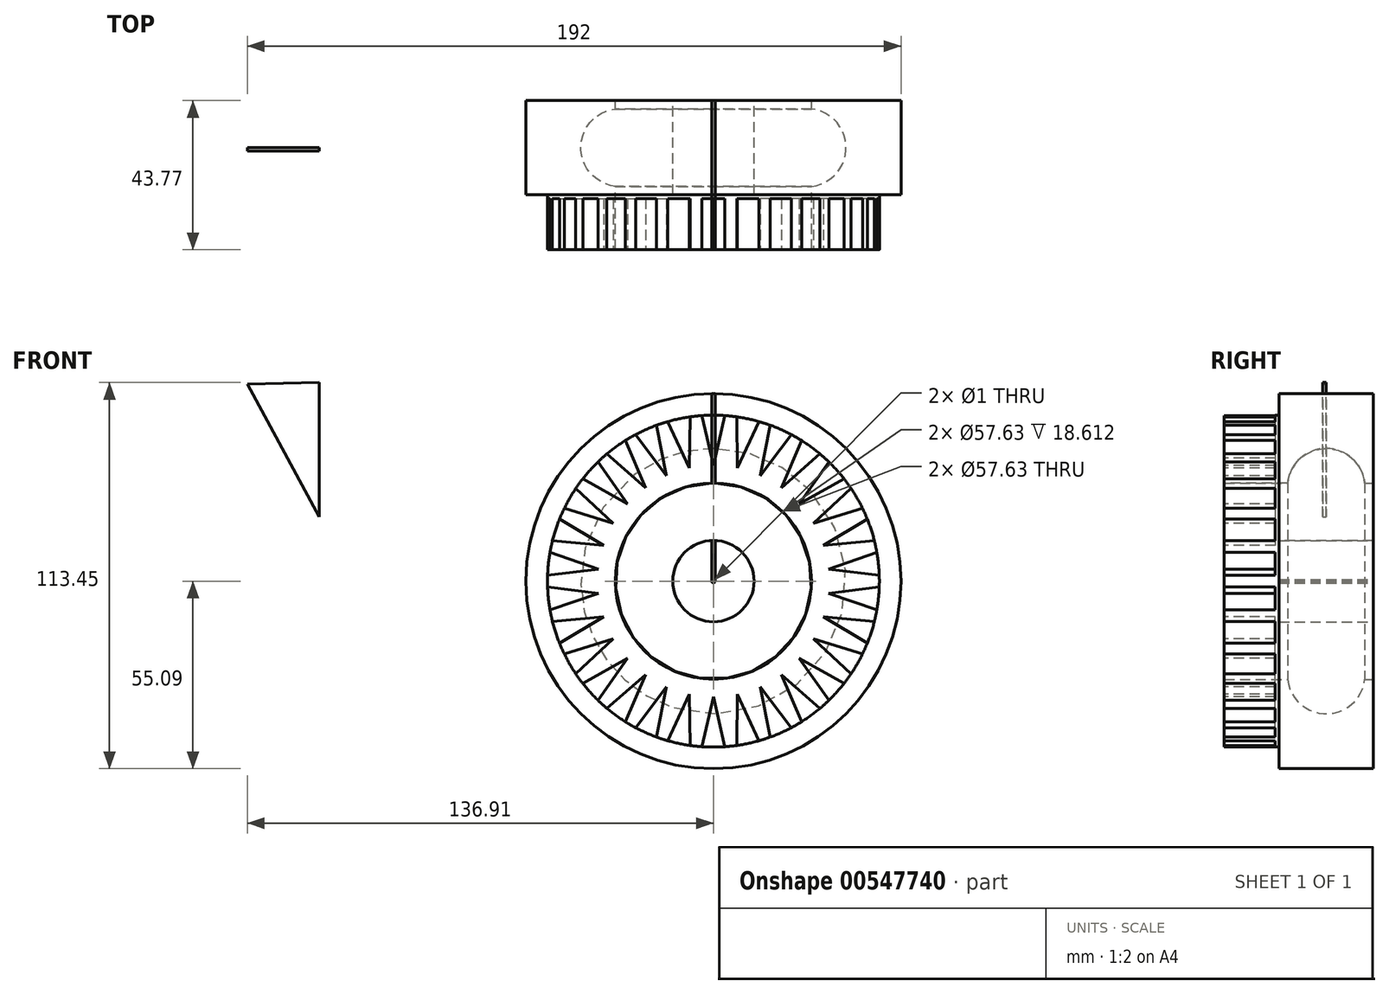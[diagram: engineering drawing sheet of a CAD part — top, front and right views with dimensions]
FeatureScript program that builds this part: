
annotation { "Feature Type Name" : "Feature", "Feature Type Description" : "" }
export const myFeature = defineFeature(function(context is Context, id is Id, definition is map)
    precondition{}
    {
        {
            var Q0;
            Q0=qCreatedBy(makeId("Right.planeOp"),FACE);
            var sketch = newSketch(context, id + "F0", { "sketchPlane" : qUnion([Q0])});
            skLineSegment(sketch, "E0.bottom", {"start": v(0, 0) * mm, "end": v(13.82, 0) * mm});
            skLineSegment(sketch, "E0.top", {"start": v(0, 26.27) * mm, "end": v(13.82, 26.27) * mm});
            skLineSegment(sketch, "E0.left", {"start": v(0, 0) * mm, "end": v(0, 26.27) * mm});
            skLineSegment(sketch, "E0.right", {"start": v(13.82, 0) * mm, "end": v(13.82, 26.27) * mm});
            skLineSegment(sketch, "E1.MirrorCS", {"start": v(0, 26.27) * mm, "end": v(-13.82, 26.27) * mm});
            skLineSegment(sketch, "E2.MirrorCS", {"start": v(-13.82, 0) * mm, "end": v(-13.82, 26.27) * mm});
            skLineSegment(sketch, "E3.MirrorCS", {"start": v(0, 0) * mm, "end": v(-13.82, 0) * mm});
            skCircle(sketch, "E4", {"center": v(0, 27.54) * mm, "radius": 11.41 * mm});
            skLineSegment(sketch, "E5.MirrorCS", {"start": v(0, 28.81) * mm, "end": v(-13.82, 28.81) * mm});
            skLineSegment(sketch, "E6.MirrorCS", {"start": v(-13.82, 55.09) * mm, "end": v(-13.82, 28.81) * mm});
            skLineSegment(sketch, "E7.MirrorCS", {"start": v(0, 28.81) * mm, "end": v(13.82, 28.81) * mm});
            skLineSegment(sketch, "E8.MirrorCS", {"start": v(13.82, 55.09) * mm, "end": v(13.82, 28.81) * mm});
            skLineSegment(sketch, "E9.MirrorCS", {"start": v(0, 55.09) * mm, "end": v(13.82, 55.09) * mm});
            skLineSegment(sketch, "E10.MirrorCS", {"start": v(0, 55.09) * mm, "end": v(-13.82, 55.09) * mm});
            skLineSegment(sketch, "E11", {"start": v(-13.82, 28.81) * mm, "end": v(-29.95, 28.81) * mm});
            skLineSegment(sketch, "E12", {"start": v(-29.95, 28.81) * mm, "end": v(-29.95, 48.74) * mm});
            skLineSegment(sketch, "E13", {"start": v(-29.95, 48.74) * mm, "end": v(-13.82, 48.74) * mm});
            skLineSegment(sketch, "E14", {"start": v(-13.82, 55.09) * mm, "end": v(-13.82, 48.74) * mm});
            skLineSegment(sketch, "E15.bottom", {"start": v(13.82, 11.94) * mm, "end": v(-13.82, 11.94) * mm});
            skLineSegment(sketch, "E15.top", {"start": v(13.82, -11.94) * mm, "end": v(-13.82, -11.94) * mm});
            skLineSegment(sketch, "E15.left", {"start": v(13.82, 11.94) * mm, "end": v(13.82, -11.94) * mm});
            skLineSegment(sketch, "E15.right", {"start": v(-13.82, 11.94) * mm, "end": v(-13.82, -11.94) * mm});
            skPoint(sketch, "E15.middle", {"position": v(0, 0) * mm});
            skSolve(sketch);
        }
        {
            var Q0;
            Q0=qCreatedBy(makeId("Right.planeOp"),FACE);
            var sketch = newSketch(context, id + "F1", { "sketchPlane" : qUnion([Q0])});
            skLineSegment(sketch, "E16", {"start": v(13.71, 0) * mm, "end": v(-13.92, 0) * mm, "construction": true});
            skSolve(sketch);
        }
        {
            var Q0;
            {var subQ0=sQuery(id+"F0.wireOp",EDGE,"E0.right");Q0=makeQuery(id+"F0.imprint","IMPRINT",FACE,{"disambiguationData":[TD([[makeQuery(id+"F0.imprint","IMPRINT",EDGE,{"derivedFrom":subQ0}),1.0]])]});}
            var Q1;
            {var subQ5=sQuery(id+"F0.wireOp",EDGE,"E2.MirrorCS");Q1=makeQuery(id+"F0.imprint","IMPRINT",FACE,{"disambiguationData":[TD([[makeQuery(id+"F0.imprint","IMPRINT",EDGE,{"derivedFrom":subQ5}),-1.0]])]});}
            var Q2;
            Q2=makeQuery(id+"F0.imprint","IMPRINT",FACE,{"disambiguationData":[TD([[makeQuery(id+"F0.imprint","IMPRINT",EDGE,{"derivedFrom":sQuery(id+"F0.wireOp",EDGE,"E6.MirrorCS")}),-1.0]])]});
            var Q3;
            {var subQ4=sQuery(id+"F0.wireOp",EDGE,"E6.MirrorCS");Q3=makeQuery(id+"F0.imprint","IMPRINT",FACE,{"disambiguationData":[TD([[makeQuery(id+"F0.imprint","IMPRINT",EDGE,{"derivedFrom":subQ4}),1.0]])]});}
            extrude(context, id + "F2", {"entities" : qUnion([Q0, Q1, Q2, Q3]), "endBound" : BoundingType.SYMMETRIC, "depth" : 1 * mm, "offsetDistance" : 25 * mm});
        }
        {
            var Q0;
            Q0=makeQuery(id+"F2.opExtrude","CAP_FACE",FACE,{"disambiguationData":[OSD([sQuery(id+"F0.wireOp",EDGE,"E4"),sQuery(id+"F0.wireOp",EDGE,"E5.MirrorCS"),sQuery(id+"F0.wireOp",EDGE,"E7.MirrorCS"),sQuery(id+"F0.wireOp",EDGE,"E8.MirrorCS"),sQuery(id+"F0.wireOp",EDGE,"E9.MirrorCS"),sQuery(id+"F0.wireOp",EDGE,"E10.MirrorCS"),sQuery(id+"F0.wireOp",EDGE,"E11"),sQuery(id+"F0.wireOp",EDGE,"E12"),sQuery(id+"F0.wireOp",EDGE,"E13"),sQuery(id+"F0.wireOp",EDGE,"E14")])],"isStart":true});
            var Q1;
            Q1=makeQuery(id+"F2.opExtrude","CAP_FACE",FACE,{"disambiguationData":[OSD([sQuery(id+"F0.wireOp",EDGE,"E0.top"),sQuery(id+"F0.wireOp",EDGE,"E0.right"),sQuery(id+"F0.wireOp",EDGE,"E1.MirrorCS"),sQuery(id+"F0.wireOp",EDGE,"E2.MirrorCS"),sQuery(id+"F0.wireOp",EDGE,"E4"),sQuery(id+"F0.wireOp",EDGE,"E15.bottom")])],"isStart":true});
            var Q2;
            Q2=sQuery(id+"F1.wireOp",EDGE,"E16");
            revolve(context, id + "F3", {"entities" : qUnion([Q0, Q1]), "axis" : qUnion([Q2]), "revolveType" : RevolveType.FULL});
        }
        {
            var Q0;
            Q0=makeQuery(id+"F3.opRevolve","SWEPT_FACE",FACE,{"disambiguationData":[OSD([sQuery(id+"F0.wireOp",EDGE,"E12")])]});
            var sketch = newSketch(context, id + "F4", { "sketchPlane" : qUnion([Q0])});
            skLineSegment(sketch, "E17", {"start": v(0, 48.74) * mm, "end": v(-3.37, 48.74) * mm});
            skLineSegment(sketch, "E18", {"start": v(-3.37, 48.74) * mm, "end": v(0, 33.93) * mm});
            skLineSegment(sketch, "E19.MirrorCS", {"start": v(0, 48.74) * mm, "end": v(3.37, 48.74) * mm});
            skPoint(sketch, "E20.center", {"position": v(0, 0) * mm});
            skLineSegment(sketch, "E21.MirrorCS", {"start": v(3.37, 48.74) * mm, "end": v(0, 33.93) * mm});
            skLineSegment(sketch, "E22.1.0", {"start": v(-6.84, 48.37) * mm, "end": v(-7.05, 33.2) * mm});
            skLineSegment(sketch, "E22.1.1", {"start": v(-13.43, 46.97) * mm, "end": v(-7.05, 33.2) * mm});
            skLineSegment(sketch, "E22.1.2", {"start": v(-10.13, 47.67) * mm, "end": v(-6.84, 48.37) * mm});
            skLineSegment(sketch, "E22.1.3", {"start": v(-10.13, 47.67) * mm, "end": v(-13.43, 46.97) * mm});
            skLineSegment(sketch, "E22.2.0", {"start": v(-16.74, 45.9) * mm, "end": v(-13.8, 31) * mm});
            skLineSegment(sketch, "E22.2.1", {"start": v(-22.9, 43.15) * mm, "end": v(-13.8, 31) * mm});
            skLineSegment(sketch, "E22.2.2", {"start": v(-19.82, 44.53) * mm, "end": v(-16.74, 45.9) * mm});
            skLineSegment(sketch, "E22.2.3", {"start": v(-19.82, 44.53) * mm, "end": v(-22.9, 43.15) * mm});
            skLineSegment(sketch, "E23.2.3.0", {"start": v(-25.92, 41.41) * mm, "end": v(-19.94, 27.45) * mm});
            skLineSegment(sketch, "E23.3.3.0", {"start": v(-31.38, 37.45) * mm, "end": v(-19.94, 27.45) * mm});
            skLineSegment(sketch, "E23.6.3.0", {"start": v(-28.65, 39.43) * mm, "end": v(-25.92, 41.41) * mm});
            skLineSegment(sketch, "E23.9.3.0", {"start": v(-28.65, 39.43) * mm, "end": v(-31.38, 37.45) * mm});
            skLineSegment(sketch, "E23.2.4.0", {"start": v(-33.96, 35.12) * mm, "end": v(-25.22, 22.7) * mm});
            skLineSegment(sketch, "E23.3.4.0", {"start": v(-38.48, 30.1) * mm, "end": v(-25.22, 22.7) * mm});
            skLineSegment(sketch, "E23.6.4.0", {"start": v(-36.22, 32.61) * mm, "end": v(-33.96, 35.12) * mm});
            skLineSegment(sketch, "E23.9.4.0", {"start": v(-36.22, 32.61) * mm, "end": v(-38.48, 30.1) * mm});
            skLineSegment(sketch, "E23.2.5.0", {"start": v(-40.52, 27.29) * mm, "end": v(-29.39, 16.97) * mm});
            skLineSegment(sketch, "E23.3.5.0", {"start": v(-43.9, 21.45) * mm, "end": v(-29.39, 16.97) * mm});
            skLineSegment(sketch, "E23.6.5.0", {"start": v(-42.2, 24.37) * mm, "end": v(-40.52, 27.29) * mm});
            skLineSegment(sketch, "E23.9.5.0", {"start": v(-42.2, 24.37) * mm, "end": v(-43.9, 21.45) * mm});
            skLineSegment(sketch, "E23.2.6.0", {"start": v(-45.31, 18.27) * mm, "end": v(-32.27, 10.49) * mm});
            skLineSegment(sketch, "E23.3.6.0", {"start": v(-47.4, 11.86) * mm, "end": v(-32.27, 10.49) * mm});
            skLineSegment(sketch, "E23.6.6.0", {"start": v(-46.35, 15.06) * mm, "end": v(-45.31, 18.27) * mm});
            skLineSegment(sketch, "E23.9.6.0", {"start": v(-46.35, 15.06) * mm, "end": v(-47.4, 11.86) * mm});
            skLineSegment(sketch, "E23.2.7.0", {"start": v(-48.12, 8.45) * mm, "end": v(-33.75, 3.55) * mm});
            skLineSegment(sketch, "E23.3.7.0", {"start": v(-48.82, 1.74) * mm, "end": v(-33.75, 3.55) * mm});
            skLineSegment(sketch, "E23.6.7.0", {"start": v(-48.47, 5.1) * mm, "end": v(-48.12, 8.45) * mm});
            skLineSegment(sketch, "E23.9.7.0", {"start": v(-48.47, 5.1) * mm, "end": v(-48.82, 1.74) * mm});
            skLineSegment(sketch, "E23.2.8.0", {"start": v(-48.82, -1.74) * mm, "end": v(-33.75, -3.55) * mm});
            skLineSegment(sketch, "E23.3.8.0", {"start": v(-48.12, -8.45) * mm, "end": v(-33.75, -3.55) * mm});
            skLineSegment(sketch, "E23.6.8.0", {"start": v(-48.47, -5.1) * mm, "end": v(-48.82, -1.74) * mm});
            skLineSegment(sketch, "E23.9.8.0", {"start": v(-48.47, -5.1) * mm, "end": v(-48.12, -8.45) * mm});
            skLineSegment(sketch, "E23.2.9.0", {"start": v(-47.4, -11.86) * mm, "end": v(-32.27, -10.49) * mm});
            skLineSegment(sketch, "E23.3.9.0", {"start": v(-45.31, -18.27) * mm, "end": v(-32.27, -10.49) * mm});
            skLineSegment(sketch, "E23.6.9.0", {"start": v(-46.35, -15.06) * mm, "end": v(-47.4, -11.86) * mm});
            skLineSegment(sketch, "E23.9.9.0", {"start": v(-46.35, -15.06) * mm, "end": v(-45.31, -18.27) * mm});
            skLineSegment(sketch, "E23.2.10.0", {"start": v(-43.9, -21.45) * mm, "end": v(-29.39, -16.97) * mm});
            skLineSegment(sketch, "E23.3.10.0", {"start": v(-40.52, -27.29) * mm, "end": v(-29.39, -16.97) * mm});
            skLineSegment(sketch, "E23.6.10.0", {"start": v(-42.2, -24.37) * mm, "end": v(-43.9, -21.45) * mm});
            skLineSegment(sketch, "E23.9.10.0", {"start": v(-42.2, -24.37) * mm, "end": v(-40.52, -27.29) * mm});
            skLineSegment(sketch, "E23.2.11.0", {"start": v(-38.48, -30.1) * mm, "end": v(-25.22, -22.7) * mm});
            skLineSegment(sketch, "E23.3.11.0", {"start": v(-33.96, -35.12) * mm, "end": v(-25.22, -22.7) * mm});
            skLineSegment(sketch, "E23.6.11.0", {"start": v(-36.22, -32.61) * mm, "end": v(-38.48, -30.1) * mm});
            skLineSegment(sketch, "E23.9.11.0", {"start": v(-36.22, -32.61) * mm, "end": v(-33.96, -35.12) * mm});
            skLineSegment(sketch, "E23.2.12.0", {"start": v(-31.38, -37.45) * mm, "end": v(-19.94, -27.45) * mm});
            skLineSegment(sketch, "E23.3.12.0", {"start": v(-25.92, -41.41) * mm, "end": v(-19.94, -27.45) * mm});
            skLineSegment(sketch, "E23.6.12.0", {"start": v(-28.65, -39.43) * mm, "end": v(-31.38, -37.45) * mm});
            skLineSegment(sketch, "E23.9.12.0", {"start": v(-28.65, -39.43) * mm, "end": v(-25.92, -41.41) * mm});
            skLineSegment(sketch, "E23.2.13.0", {"start": v(-22.9, -43.15) * mm, "end": v(-13.8, -31) * mm});
            skLineSegment(sketch, "E23.3.13.0", {"start": v(-16.74, -45.9) * mm, "end": v(-13.8, -31) * mm});
            skLineSegment(sketch, "E23.6.13.0", {"start": v(-19.82, -44.53) * mm, "end": v(-22.9, -43.15) * mm});
            skLineSegment(sketch, "E23.9.13.0", {"start": v(-19.82, -44.53) * mm, "end": v(-16.74, -45.9) * mm});
            skLineSegment(sketch, "E23.2.14.0", {"start": v(-13.43, -46.97) * mm, "end": v(-7.05, -33.2) * mm});
            skLineSegment(sketch, "E23.3.14.0", {"start": v(-6.84, -48.37) * mm, "end": v(-7.05, -33.2) * mm});
            skLineSegment(sketch, "E23.6.14.0", {"start": v(-10.13, -47.67) * mm, "end": v(-13.43, -46.97) * mm});
            skLineSegment(sketch, "E23.9.14.0", {"start": v(-10.13, -47.67) * mm, "end": v(-6.84, -48.37) * mm});
            skLineSegment(sketch, "E23.2.15.0", {"start": v(-3.37, -48.74) * mm, "end": v(0, -33.93) * mm});
            skLineSegment(sketch, "E23.3.15.0", {"start": v(3.37, -48.74) * mm, "end": v(0, -33.93) * mm});
            skLineSegment(sketch, "E23.6.15.0", {"start": v(0, -48.74) * mm, "end": v(-3.37, -48.74) * mm});
            skLineSegment(sketch, "E23.9.15.0", {"start": v(0, -48.74) * mm, "end": v(3.37, -48.74) * mm});
            skLineSegment(sketch, "E23.2.16.0", {"start": v(6.84, -48.37) * mm, "end": v(7.05, -33.2) * mm});
            skLineSegment(sketch, "E23.3.16.0", {"start": v(13.43, -46.97) * mm, "end": v(7.05, -33.2) * mm});
            skLineSegment(sketch, "E23.6.16.0", {"start": v(10.13, -47.67) * mm, "end": v(6.84, -48.37) * mm});
            skLineSegment(sketch, "E23.9.16.0", {"start": v(10.13, -47.67) * mm, "end": v(13.43, -46.97) * mm});
            skLineSegment(sketch, "E23.2.17.0", {"start": v(16.74, -45.9) * mm, "end": v(13.8, -31) * mm});
            skLineSegment(sketch, "E23.3.17.0", {"start": v(22.9, -43.15) * mm, "end": v(13.8, -31) * mm});
            skLineSegment(sketch, "E23.6.17.0", {"start": v(19.82, -44.53) * mm, "end": v(16.74, -45.9) * mm});
            skLineSegment(sketch, "E23.9.17.0", {"start": v(19.82, -44.53) * mm, "end": v(22.9, -43.15) * mm});
            skLineSegment(sketch, "E23.2.18.0", {"start": v(25.92, -41.41) * mm, "end": v(19.94, -27.45) * mm});
            skLineSegment(sketch, "E23.3.18.0", {"start": v(31.38, -37.45) * mm, "end": v(19.94, -27.45) * mm});
            skLineSegment(sketch, "E23.6.18.0", {"start": v(28.65, -39.43) * mm, "end": v(25.92, -41.41) * mm});
            skLineSegment(sketch, "E23.9.18.0", {"start": v(28.65, -39.43) * mm, "end": v(31.38, -37.45) * mm});
            skLineSegment(sketch, "E23.2.19.0", {"start": v(33.96, -35.12) * mm, "end": v(25.22, -22.7) * mm});
            skLineSegment(sketch, "E23.3.19.0", {"start": v(38.48, -30.1) * mm, "end": v(25.22, -22.7) * mm});
            skLineSegment(sketch, "E23.6.19.0", {"start": v(36.22, -32.61) * mm, "end": v(33.96, -35.12) * mm});
            skLineSegment(sketch, "E23.9.19.0", {"start": v(36.22, -32.61) * mm, "end": v(38.48, -30.1) * mm});
            skLineSegment(sketch, "E23.2.20.0", {"start": v(40.52, -27.29) * mm, "end": v(29.39, -16.97) * mm});
            skLineSegment(sketch, "E23.3.20.0", {"start": v(43.9, -21.45) * mm, "end": v(29.39, -16.97) * mm});
            skLineSegment(sketch, "E23.6.20.0", {"start": v(42.2, -24.37) * mm, "end": v(40.52, -27.29) * mm});
            skLineSegment(sketch, "E23.9.20.0", {"start": v(42.2, -24.37) * mm, "end": v(43.9, -21.45) * mm});
            skLineSegment(sketch, "E23.2.21.0", {"start": v(45.31, -18.27) * mm, "end": v(32.27, -10.49) * mm});
            skLineSegment(sketch, "E23.3.21.0", {"start": v(47.4, -11.86) * mm, "end": v(32.27, -10.49) * mm});
            skLineSegment(sketch, "E23.6.21.0", {"start": v(46.35, -15.06) * mm, "end": v(45.31, -18.27) * mm});
            skLineSegment(sketch, "E23.9.21.0", {"start": v(46.35, -15.06) * mm, "end": v(47.4, -11.86) * mm});
            skLineSegment(sketch, "E23.2.22.0", {"start": v(48.12, -8.45) * mm, "end": v(33.75, -3.55) * mm});
            skLineSegment(sketch, "E23.3.22.0", {"start": v(48.82, -1.74) * mm, "end": v(33.75, -3.55) * mm});
            skLineSegment(sketch, "E23.6.22.0", {"start": v(48.47, -5.1) * mm, "end": v(48.12, -8.45) * mm});
            skLineSegment(sketch, "E23.9.22.0", {"start": v(48.47, -5.1) * mm, "end": v(48.82, -1.74) * mm});
            skLineSegment(sketch, "E23.2.23.0", {"start": v(48.82, 1.74) * mm, "end": v(33.75, 3.55) * mm});
            skLineSegment(sketch, "E23.3.23.0", {"start": v(48.12, 8.45) * mm, "end": v(33.75, 3.55) * mm});
            skLineSegment(sketch, "E23.6.23.0", {"start": v(48.47, 5.1) * mm, "end": v(48.82, 1.74) * mm});
            skLineSegment(sketch, "E23.9.23.0", {"start": v(48.47, 5.1) * mm, "end": v(48.12, 8.45) * mm});
            skLineSegment(sketch, "E23.2.24.0", {"start": v(47.4, 11.86) * mm, "end": v(32.27, 10.49) * mm});
            skLineSegment(sketch, "E23.3.24.0", {"start": v(45.31, 18.27) * mm, "end": v(32.27, 10.49) * mm});
            skLineSegment(sketch, "E23.6.24.0", {"start": v(46.35, 15.06) * mm, "end": v(47.4, 11.86) * mm});
            skLineSegment(sketch, "E23.9.24.0", {"start": v(46.35, 15.06) * mm, "end": v(45.31, 18.27) * mm});
            skLineSegment(sketch, "E23.2.25.0", {"start": v(43.9, 21.45) * mm, "end": v(29.39, 16.97) * mm});
            skLineSegment(sketch, "E23.3.25.0", {"start": v(40.52, 27.29) * mm, "end": v(29.39, 16.97) * mm});
            skLineSegment(sketch, "E23.6.25.0", {"start": v(42.2, 24.37) * mm, "end": v(43.9, 21.45) * mm});
            skLineSegment(sketch, "E23.9.25.0", {"start": v(42.2, 24.37) * mm, "end": v(40.52, 27.29) * mm});
            skLineSegment(sketch, "E23.2.26.0", {"start": v(38.48, 30.1) * mm, "end": v(25.22, 22.7) * mm});
            skLineSegment(sketch, "E23.3.26.0", {"start": v(33.96, 35.12) * mm, "end": v(25.22, 22.7) * mm});
            skLineSegment(sketch, "E23.6.26.0", {"start": v(36.22, 32.61) * mm, "end": v(38.48, 30.1) * mm});
            skLineSegment(sketch, "E23.9.26.0", {"start": v(36.22, 32.61) * mm, "end": v(33.96, 35.12) * mm});
            skLineSegment(sketch, "E23.2.27.0", {"start": v(31.38, 37.45) * mm, "end": v(19.94, 27.45) * mm});
            skLineSegment(sketch, "E23.3.27.0", {"start": v(25.92, 41.41) * mm, "end": v(19.94, 27.45) * mm});
            skLineSegment(sketch, "E23.6.27.0", {"start": v(28.65, 39.43) * mm, "end": v(31.38, 37.45) * mm});
            skLineSegment(sketch, "E23.9.27.0", {"start": v(28.65, 39.43) * mm, "end": v(25.92, 41.41) * mm});
            skLineSegment(sketch, "E23.2.28.0", {"start": v(22.9, 43.15) * mm, "end": v(13.8, 31) * mm});
            skLineSegment(sketch, "E23.3.28.0", {"start": v(16.74, 45.9) * mm, "end": v(13.8, 31) * mm});
            skLineSegment(sketch, "E23.6.28.0", {"start": v(19.82, 44.53) * mm, "end": v(22.9, 43.15) * mm});
            skLineSegment(sketch, "E23.9.28.0", {"start": v(19.82, 44.53) * mm, "end": v(16.74, 45.9) * mm});
            skLineSegment(sketch, "E23.2.29.0", {"start": v(13.43, 46.97) * mm, "end": v(7.05, 33.2) * mm});
            skLineSegment(sketch, "E23.3.29.0", {"start": v(6.84, 48.37) * mm, "end": v(7.05, 33.2) * mm});
            skLineSegment(sketch, "E23.6.29.0", {"start": v(10.13, 47.67) * mm, "end": v(13.43, 46.97) * mm});
            skLineSegment(sketch, "E23.9.29.0", {"start": v(10.13, 47.67) * mm, "end": v(6.84, 48.37) * mm});
            skSolve(sketch);
        }
        {
            var Q0;
            {var subQ0=sQuery(id+"F4.wireOp",EDGE,"E22.1.1");var subQ1=sQuery(id+"F4.wireOp",EDGE,"E22.1.0");var subQ2=makeQuery(id+"F4.imprint","INTERSECT",VERTEX,{"derivedFrom":[subQ1,subQ0]});Q0=makeQuery(id+"F4.imprint","IMPRINT",FACE,{"disambiguationData":[TD([[makeQuery(id+"F4.imprint","IMPRINT",EDGE,{"disambiguationData":[TD([[subQ2,1.0]])],"derivedFrom":subQ1}),-1.0]])]});}
            var Q1;
            {var subQ0=sQuery(id+"F4.wireOp",EDGE,"E21.MirrorCS");var subQ1=sQuery(id+"F4.wireOp",EDGE,"E18");var subQ2=makeQuery(id+"F4.imprint","INTERSECT",VERTEX,{"derivedFrom":[subQ1,subQ0]});Q1=makeQuery(id+"F4.imprint","IMPRINT",FACE,{"disambiguationData":[TD([[makeQuery(id+"F4.imprint","IMPRINT",EDGE,{"disambiguationData":[TD([[subQ2,1.0]])],"derivedFrom":subQ1}),1.0]])]});}
            var Q2;
            {var subQ0=sQuery(id+"F4.wireOp",EDGE,"E23.3.29.0");var subQ1=sQuery(id+"F4.wireOp",EDGE,"E23.2.29.0");var subQ2=makeQuery(id+"F4.imprint","INTERSECT",VERTEX,{"derivedFrom":[subQ1,subQ0]});Q2=makeQuery(id+"F4.imprint","IMPRINT",FACE,{"disambiguationData":[TD([[makeQuery(id+"F4.imprint","IMPRINT",EDGE,{"disambiguationData":[TD([[subQ2,1.0]])],"derivedFrom":subQ1}),-1.0]])]});}
            var Q3;
            {var subQ0=sQuery(id+"F4.wireOp",EDGE,"E23.3.28.0");var subQ1=sQuery(id+"F4.wireOp",EDGE,"E23.2.28.0");var subQ2=makeQuery(id+"F4.imprint","INTERSECT",VERTEX,{"derivedFrom":[subQ1,subQ0]});Q3=makeQuery(id+"F4.imprint","IMPRINT",FACE,{"disambiguationData":[TD([[makeQuery(id+"F4.imprint","IMPRINT",EDGE,{"disambiguationData":[TD([[subQ2,1.0]])],"derivedFrom":subQ1}),-1.0]])]});}
            var Q4;
            {var subQ0=sQuery(id+"F4.wireOp",EDGE,"E23.3.27.0");var subQ1=sQuery(id+"F4.wireOp",EDGE,"E23.2.27.0");var subQ2=makeQuery(id+"F4.imprint","INTERSECT",VERTEX,{"derivedFrom":[subQ1,subQ0]});Q4=makeQuery(id+"F4.imprint","IMPRINT",FACE,{"disambiguationData":[TD([[makeQuery(id+"F4.imprint","IMPRINT",EDGE,{"disambiguationData":[TD([[subQ2,1.0]])],"derivedFrom":subQ1}),-1.0]])]});}
            var Q5;
            {var subQ0=sQuery(id+"F4.wireOp",EDGE,"E23.3.26.0");var subQ1=sQuery(id+"F4.wireOp",EDGE,"E23.2.26.0");var subQ2=makeQuery(id+"F4.imprint","INTERSECT",VERTEX,{"derivedFrom":[subQ1,subQ0]});Q5=makeQuery(id+"F4.imprint","IMPRINT",FACE,{"disambiguationData":[TD([[makeQuery(id+"F4.imprint","IMPRINT",EDGE,{"disambiguationData":[TD([[subQ2,1.0]])],"derivedFrom":subQ1}),-1.0]])]});}
            var Q6;
            {var subQ0=sQuery(id+"F4.wireOp",EDGE,"E23.3.25.0");var subQ1=sQuery(id+"F4.wireOp",EDGE,"E23.2.25.0");var subQ2=makeQuery(id+"F4.imprint","INTERSECT",VERTEX,{"derivedFrom":[subQ1,subQ0]});Q6=makeQuery(id+"F4.imprint","IMPRINT",FACE,{"disambiguationData":[TD([[makeQuery(id+"F4.imprint","IMPRINT",EDGE,{"disambiguationData":[TD([[subQ2,1.0]])],"derivedFrom":subQ1}),-1.0]])]});}
            var Q7;
            {var subQ0=sQuery(id+"F4.wireOp",EDGE,"E23.3.24.0");var subQ1=sQuery(id+"F4.wireOp",EDGE,"E23.2.24.0");var subQ2=makeQuery(id+"F4.imprint","INTERSECT",VERTEX,{"derivedFrom":[subQ1,subQ0]});Q7=makeQuery(id+"F4.imprint","IMPRINT",FACE,{"disambiguationData":[TD([[makeQuery(id+"F4.imprint","IMPRINT",EDGE,{"disambiguationData":[TD([[subQ2,1.0]])],"derivedFrom":subQ1}),-1.0]])]});}
            var Q8;
            {var subQ0=sQuery(id+"F4.wireOp",EDGE,"E23.3.23.0");var subQ1=sQuery(id+"F4.wireOp",EDGE,"E23.2.23.0");var subQ2=makeQuery(id+"F4.imprint","INTERSECT",VERTEX,{"derivedFrom":[subQ1,subQ0]});Q8=makeQuery(id+"F4.imprint","IMPRINT",FACE,{"disambiguationData":[TD([[makeQuery(id+"F4.imprint","IMPRINT",EDGE,{"disambiguationData":[TD([[subQ2,1.0]])],"derivedFrom":subQ1}),-1.0]])]});}
            var Q9;
            {var subQ0=sQuery(id+"F4.wireOp",EDGE,"E23.3.22.0");var subQ1=sQuery(id+"F4.wireOp",EDGE,"E23.2.22.0");var subQ2=makeQuery(id+"F4.imprint","INTERSECT",VERTEX,{"derivedFrom":[subQ1,subQ0]});Q9=makeQuery(id+"F4.imprint","IMPRINT",FACE,{"disambiguationData":[TD([[makeQuery(id+"F4.imprint","IMPRINT",EDGE,{"disambiguationData":[TD([[subQ2,1.0]])],"derivedFrom":subQ1}),-1.0]])]});}
            var Q10;
            {var subQ0=sQuery(id+"F4.wireOp",EDGE,"E23.3.21.0");var subQ1=sQuery(id+"F4.wireOp",EDGE,"E23.2.21.0");var subQ2=makeQuery(id+"F4.imprint","INTERSECT",VERTEX,{"derivedFrom":[subQ1,subQ0]});Q10=makeQuery(id+"F4.imprint","IMPRINT",FACE,{"disambiguationData":[TD([[makeQuery(id+"F4.imprint","IMPRINT",EDGE,{"disambiguationData":[TD([[subQ2,1.0]])],"derivedFrom":subQ1}),-1.0]])]});}
            var Q11;
            {var subQ0=sQuery(id+"F4.wireOp",EDGE,"E23.3.20.0");var subQ1=sQuery(id+"F4.wireOp",EDGE,"E23.2.20.0");var subQ2=makeQuery(id+"F4.imprint","INTERSECT",VERTEX,{"derivedFrom":[subQ1,subQ0]});Q11=makeQuery(id+"F4.imprint","IMPRINT",FACE,{"disambiguationData":[TD([[makeQuery(id+"F4.imprint","IMPRINT",EDGE,{"disambiguationData":[TD([[subQ2,1.0]])],"derivedFrom":subQ1}),-1.0]])]});}
            var Q12;
            {var subQ0=sQuery(id+"F4.wireOp",EDGE,"E23.3.19.0");var subQ1=sQuery(id+"F4.wireOp",EDGE,"E23.2.19.0");var subQ2=makeQuery(id+"F4.imprint","INTERSECT",VERTEX,{"derivedFrom":[subQ1,subQ0]});Q12=makeQuery(id+"F4.imprint","IMPRINT",FACE,{"disambiguationData":[TD([[makeQuery(id+"F4.imprint","IMPRINT",EDGE,{"disambiguationData":[TD([[subQ2,1.0]])],"derivedFrom":subQ1}),-1.0]])]});}
            var Q13;
            {var subQ0=sQuery(id+"F4.wireOp",EDGE,"E23.3.18.0");var subQ1=sQuery(id+"F4.wireOp",EDGE,"E23.2.18.0");var subQ2=makeQuery(id+"F4.imprint","INTERSECT",VERTEX,{"derivedFrom":[subQ1,subQ0]});Q13=makeQuery(id+"F4.imprint","IMPRINT",FACE,{"disambiguationData":[TD([[makeQuery(id+"F4.imprint","IMPRINT",EDGE,{"disambiguationData":[TD([[subQ2,1.0]])],"derivedFrom":subQ1}),-1.0]])]});}
            var Q14;
            {var subQ0=sQuery(id+"F4.wireOp",EDGE,"E23.3.17.0");var subQ1=sQuery(id+"F4.wireOp",EDGE,"E23.2.17.0");var subQ2=makeQuery(id+"F4.imprint","INTERSECT",VERTEX,{"derivedFrom":[subQ1,subQ0]});Q14=makeQuery(id+"F4.imprint","IMPRINT",FACE,{"disambiguationData":[TD([[makeQuery(id+"F4.imprint","IMPRINT",EDGE,{"disambiguationData":[TD([[subQ2,1.0]])],"derivedFrom":subQ1}),-1.0]])]});}
            var Q15;
            {var subQ0=sQuery(id+"F4.wireOp",EDGE,"E23.3.16.0");var subQ1=sQuery(id+"F4.wireOp",EDGE,"E23.2.16.0");var subQ2=makeQuery(id+"F4.imprint","INTERSECT",VERTEX,{"derivedFrom":[subQ1,subQ0]});Q15=makeQuery(id+"F4.imprint","IMPRINT",FACE,{"disambiguationData":[TD([[makeQuery(id+"F4.imprint","IMPRINT",EDGE,{"disambiguationData":[TD([[subQ2,1.0]])],"derivedFrom":subQ1}),-1.0]])]});}
            var Q16;
            {var subQ0=sQuery(id+"F4.wireOp",EDGE,"E23.3.15.0");var subQ1=sQuery(id+"F4.wireOp",EDGE,"E23.2.15.0");var subQ2=makeQuery(id+"F4.imprint","INTERSECT",VERTEX,{"derivedFrom":[subQ1,subQ0]});Q16=makeQuery(id+"F4.imprint","IMPRINT",FACE,{"disambiguationData":[TD([[makeQuery(id+"F4.imprint","IMPRINT",EDGE,{"disambiguationData":[TD([[subQ2,1.0]])],"derivedFrom":subQ1}),-1.0]])]});}
            var Q17;
            {var subQ0=sQuery(id+"F4.wireOp",EDGE,"E23.3.14.0");var subQ1=sQuery(id+"F4.wireOp",EDGE,"E23.2.14.0");var subQ2=makeQuery(id+"F4.imprint","INTERSECT",VERTEX,{"derivedFrom":[subQ1,subQ0]});Q17=makeQuery(id+"F4.imprint","IMPRINT",FACE,{"disambiguationData":[TD([[makeQuery(id+"F4.imprint","IMPRINT",EDGE,{"disambiguationData":[TD([[subQ2,1.0]])],"derivedFrom":subQ1}),-1.0]])]});}
            var Q18;
            {var subQ0=sQuery(id+"F4.wireOp",EDGE,"E23.3.13.0");var subQ1=sQuery(id+"F4.wireOp",EDGE,"E23.2.13.0");var subQ2=makeQuery(id+"F4.imprint","INTERSECT",VERTEX,{"derivedFrom":[subQ1,subQ0]});Q18=makeQuery(id+"F4.imprint","IMPRINT",FACE,{"disambiguationData":[TD([[makeQuery(id+"F4.imprint","IMPRINT",EDGE,{"disambiguationData":[TD([[subQ2,1.0]])],"derivedFrom":subQ1}),-1.0]])]});}
            var Q19;
            {var subQ0=sQuery(id+"F4.wireOp",EDGE,"E23.3.12.0");var subQ1=sQuery(id+"F4.wireOp",EDGE,"E23.2.12.0");var subQ2=makeQuery(id+"F4.imprint","INTERSECT",VERTEX,{"derivedFrom":[subQ1,subQ0]});Q19=makeQuery(id+"F4.imprint","IMPRINT",FACE,{"disambiguationData":[TD([[makeQuery(id+"F4.imprint","IMPRINT",EDGE,{"disambiguationData":[TD([[subQ2,1.0]])],"derivedFrom":subQ1}),-1.0]])]});}
            var Q20;
            {var subQ0=sQuery(id+"F4.wireOp",EDGE,"E23.3.11.0");var subQ1=sQuery(id+"F4.wireOp",EDGE,"E23.2.11.0");var subQ2=makeQuery(id+"F4.imprint","INTERSECT",VERTEX,{"derivedFrom":[subQ1,subQ0]});Q20=makeQuery(id+"F4.imprint","IMPRINT",FACE,{"disambiguationData":[TD([[makeQuery(id+"F4.imprint","IMPRINT",EDGE,{"disambiguationData":[TD([[subQ2,1.0]])],"derivedFrom":subQ1}),-1.0]])]});}
            var Q21;
            {var subQ0=sQuery(id+"F4.wireOp",EDGE,"E23.3.10.0");var subQ1=sQuery(id+"F4.wireOp",EDGE,"E23.2.10.0");var subQ2=makeQuery(id+"F4.imprint","INTERSECT",VERTEX,{"derivedFrom":[subQ1,subQ0]});Q21=makeQuery(id+"F4.imprint","IMPRINT",FACE,{"disambiguationData":[TD([[makeQuery(id+"F4.imprint","IMPRINT",EDGE,{"disambiguationData":[TD([[subQ2,1.0]])],"derivedFrom":subQ1}),-1.0]])]});}
            var Q22;
            {var subQ0=sQuery(id+"F4.wireOp",EDGE,"E23.3.9.0");var subQ1=sQuery(id+"F4.wireOp",EDGE,"E23.2.9.0");var subQ2=makeQuery(id+"F4.imprint","INTERSECT",VERTEX,{"derivedFrom":[subQ1,subQ0]});Q22=makeQuery(id+"F4.imprint","IMPRINT",FACE,{"disambiguationData":[TD([[makeQuery(id+"F4.imprint","IMPRINT",EDGE,{"disambiguationData":[TD([[subQ2,1.0]])],"derivedFrom":subQ1}),-1.0]])]});}
            var Q23;
            {var subQ0=sQuery(id+"F4.wireOp",EDGE,"E23.3.8.0");var subQ1=sQuery(id+"F4.wireOp",EDGE,"E23.2.8.0");var subQ2=makeQuery(id+"F4.imprint","INTERSECT",VERTEX,{"derivedFrom":[subQ1,subQ0]});Q23=makeQuery(id+"F4.imprint","IMPRINT",FACE,{"disambiguationData":[TD([[makeQuery(id+"F4.imprint","IMPRINT",EDGE,{"disambiguationData":[TD([[subQ2,1.0]])],"derivedFrom":subQ1}),-1.0]])]});}
            var Q24;
            {var subQ0=sQuery(id+"F4.wireOp",EDGE,"E23.3.7.0");var subQ1=sQuery(id+"F4.wireOp",EDGE,"E23.2.7.0");var subQ2=makeQuery(id+"F4.imprint","INTERSECT",VERTEX,{"derivedFrom":[subQ1,subQ0]});Q24=makeQuery(id+"F4.imprint","IMPRINT",FACE,{"disambiguationData":[TD([[makeQuery(id+"F4.imprint","IMPRINT",EDGE,{"disambiguationData":[TD([[subQ2,1.0]])],"derivedFrom":subQ1}),-1.0]])]});}
            var Q25;
            {var subQ0=sQuery(id+"F4.wireOp",EDGE,"E23.3.6.0");var subQ1=sQuery(id+"F4.wireOp",EDGE,"E23.2.6.0");var subQ2=makeQuery(id+"F4.imprint","INTERSECT",VERTEX,{"derivedFrom":[subQ1,subQ0]});Q25=makeQuery(id+"F4.imprint","IMPRINT",FACE,{"disambiguationData":[TD([[makeQuery(id+"F4.imprint","IMPRINT",EDGE,{"disambiguationData":[TD([[subQ2,1.0]])],"derivedFrom":subQ1}),-1.0]])]});}
            var Q26;
            {var subQ0=sQuery(id+"F4.wireOp",EDGE,"E23.3.5.0");var subQ1=sQuery(id+"F4.wireOp",EDGE,"E23.2.5.0");var subQ2=makeQuery(id+"F4.imprint","INTERSECT",VERTEX,{"derivedFrom":[subQ1,subQ0]});Q26=makeQuery(id+"F4.imprint","IMPRINT",FACE,{"disambiguationData":[TD([[makeQuery(id+"F4.imprint","IMPRINT",EDGE,{"disambiguationData":[TD([[subQ2,1.0]])],"derivedFrom":subQ1}),-1.0]])]});}
            var Q27;
            {var subQ0=sQuery(id+"F4.wireOp",EDGE,"E23.3.4.0");var subQ1=sQuery(id+"F4.wireOp",EDGE,"E23.2.4.0");var subQ2=makeQuery(id+"F4.imprint","INTERSECT",VERTEX,{"derivedFrom":[subQ1,subQ0]});Q27=makeQuery(id+"F4.imprint","IMPRINT",FACE,{"disambiguationData":[TD([[makeQuery(id+"F4.imprint","IMPRINT",EDGE,{"disambiguationData":[TD([[subQ2,1.0]])],"derivedFrom":subQ1}),-1.0]])]});}
            var Q28;
            {var subQ0=sQuery(id+"F4.wireOp",EDGE,"E23.3.3.0");var subQ1=sQuery(id+"F4.wireOp",EDGE,"E23.2.3.0");var subQ2=makeQuery(id+"F4.imprint","INTERSECT",VERTEX,{"derivedFrom":[subQ1,subQ0]});Q28=makeQuery(id+"F4.imprint","IMPRINT",FACE,{"disambiguationData":[TD([[makeQuery(id+"F4.imprint","IMPRINT",EDGE,{"disambiguationData":[TD([[subQ2,1.0]])],"derivedFrom":subQ1}),-1.0]])]});}
            var Q29;
            {var subQ0=sQuery(id+"F4.wireOp",EDGE,"E22.2.1");var subQ1=sQuery(id+"F4.wireOp",EDGE,"E22.2.0");var subQ2=makeQuery(id+"F4.imprint","INTERSECT",VERTEX,{"derivedFrom":[subQ1,subQ0]});Q29=makeQuery(id+"F4.imprint","IMPRINT",FACE,{"disambiguationData":[TD([[makeQuery(id+"F4.imprint","IMPRINT",EDGE,{"disambiguationData":[TD([[subQ2,1.0]])],"derivedFrom":subQ1}),-1.0]])]});}
            extrude(context, id + "F5", {"entities" : qUnion([Q0, Q1, Q2, Q3, Q4, Q5, Q6, Q7, Q8, Q9, Q10, Q11, Q12, Q13, Q14, Q15, Q16, Q17, Q18, Q19, Q20, Q21, Q22, Q23, Q24, Q25, Q26, Q27, Q28, Q29]), "operationType" : NewBodyOperationType.REMOVE, "oppositeDirection" : true, "depth" : 15 * mm, "offsetDistance" : 25 * mm});
        }
        {
            var Q0;
            Q0=qCreatedBy(makeId("Front.planeOp"),FACE);
            var sketch = newSketch(context, id + "F6", { "sketchPlane" : qUnion([Q0])});
            skLineSegment(sketch, "E24", {"start": v(-136.9, 57.92) * mm, "end": v(-115.84, 18.87) * mm});
            skLineSegment(sketch, "E25", {"start": v(-115.84, 18.87) * mm, "end": v(-115.84, 58.36) * mm});
            skLineSegment(sketch, "E26", {"start": v(-115.84, 58.36) * mm, "end": v(-136.9, 57.92) * mm});
            skSolve(sketch);
        }
        {
            var Q0;
            Q0=makeQuery(id+"F6.imprint","IMPRINT",FACE,{"disambiguationData":[TD([[makeQuery(id+"F6.imprint","IMPRINT",EDGE,{"derivedFrom":sQuery(id+"F6.wireOp",EDGE,"E24")}),1.0]])]});
            extrude(context, id + "F7", {"entities" : qUnion([Q0]), "depth" : 1 * mm, "offsetDistance" : 25 * mm});
        }
    });
